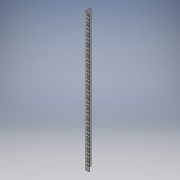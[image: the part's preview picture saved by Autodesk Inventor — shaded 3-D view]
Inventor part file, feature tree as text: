
AUTODESK INVENTOR PART (.ipt)
format: ipt  version: 2016 (Build 200138000, 138)  size: 432,128 bytes
history: native  units: in
note: dims shown in document units (in); Inventor stores cm internally (conversion verified against a paired STEP export)
features: sheet_metal_op x2, sketch x2, other x1
ambient origin geometry x8: Origin, YZ Plane, XZ Plane, XY Plane, X Axis, Y Axis, Z Axis, Center Point
bodies: Solid1 (feature_tree)
feature tree (5):
  sheet_metal_op  "Face1"
  sheet_metal_op  "Fold1"
  sketch  "Sketch1"  dims[d0=1.9685in]
  other  "Plate1"
  sketch  "Sketch4"  dims[d1=26.4173in d2=0.3937in d3=0.3937in d4=0.3937in d5=0.3937in d8=0.1181in d9=0.0787in d10=0.0531in d11=0.0236in d12=0.0236in d13=0.0236in d14=0.0236in d21=0.0787in d22=0.3937in d23=0.2047in d24=0.4599in d25=1.6437in d26=0.2313in d27=0.2313in d28=5.9055in d30=1.75in d31=0.3937in d33=0.3937in d35=0.0787in d37=1.1614in d38=0.0787in d39=0.0394in d40=0.1575in d41=0.0787in d42=90.0deg d43=0.0984in]
